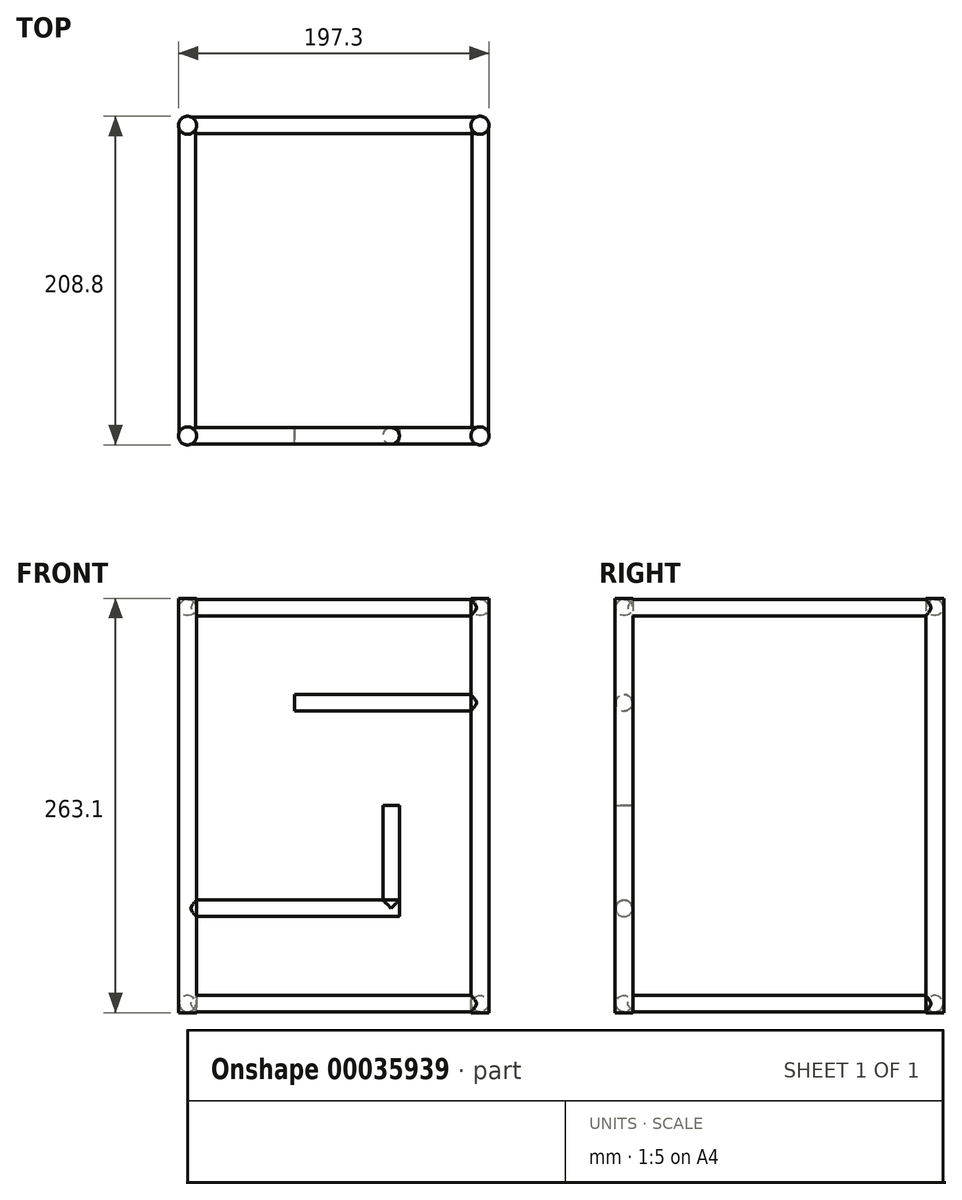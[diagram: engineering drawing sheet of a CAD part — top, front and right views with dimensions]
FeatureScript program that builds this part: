
annotation { "Feature Type Name" : "Feature", "Feature Type Description" : "" }
export const myFeature = defineFeature(function(context is Context, id is Id, definition is map)
    precondition{}
    {
        {
            var Q0;
            Q0=qCreatedBy(makeId("Front.planeOp"),FACE);
            var sketch = newSketch(context, id + "F0", { "sketchPlane" : qUnion([Q0])});
            skLineSegment(sketch, "E0.rect.bottom", {"start": v(98.65, -131.55) * mm, "end": v(-98.65, -131.55) * mm, "construction": true});
            skLineSegment(sketch, "E0.rect.top", {"start": v(98.65, 131.55) * mm, "end": v(-98.65, 131.55) * mm, "construction": true});
            skLineSegment(sketch, "E0.rect.left", {"start": v(98.65, -131.55) * mm, "end": v(98.65, 131.55) * mm, "construction": true});
            skLineSegment(sketch, "E0.rect.right", {"start": v(-98.65, -131.55) * mm, "end": v(-98.65, 131.55) * mm, "construction": true});
            skPoint(sketch, "E0.rect.middle", {"position": v(0, 0) * mm});
            skLineSegment(sketch, "E1.rect.bottom", {"start": v(87.15, -120.05) * mm, "end": v(-87.15, -120.05) * mm, "construction": true});
            skLineSegment(sketch, "E1.rect.top", {"start": v(87.15, 120.05) * mm, "end": v(-87.15, 120.05) * mm, "construction": true});
            skLineSegment(sketch, "E1.rect.left", {"start": v(87.15, -120.05) * mm, "end": v(87.15, 120.05) * mm, "construction": true});
            skLineSegment(sketch, "E1.rect.right", {"start": v(-87.15, -120.05) * mm, "end": v(-87.15, 120.05) * mm, "construction": true});
            skSolve(sketch);
        }
        {
            var Q0;
            Q0=sQuery(id+"F0.wireOp",VERTEX,"E0.rect.bottom.start");
            var Q1;
            Q1=qCreatedBy(makeId("Top.planeOp"),FACE);
            cPlane(context, id + "F1", {"entities" : qUnion([Q0, Q1]), "cplaneType" : CPlaneType.PLANE_POINT, "offset" : 150 * mm, "width" : 150 * mm, "height" : 150 * mm});
        }
        {
            var Q0;
            Q0=qCreatedBy(id+"F1.planeOp",FACE);
            var sketch = newSketch(context, id + "F2", { "sketchPlane" : qUnion([Q0])});
            skCircle(sketch, "E2", {"center": v(-92.9, 0) * mm, "radius": 5.75 * mm});
            skPoint(sketch, "E3", {"position": v(-98.65, 0) * mm});
            skPoint(sketch, "E4", {"position": v(-87.15, 0) * mm});
            skSolve(sketch);
        }
        {
            var Q0;
            Q0=makeQuery(id+"F2.imprint","IMPRINT",FACE,{"disambiguationData":[TD([[makeQuery(id+"F2.imprint","IMPRINT",EDGE,{"derivedFrom":sQuery(id+"F2.wireOp",EDGE,"E2")}),1.0]])]});
            extrude(context, id + "F3", {"entities" : qUnion([Q0]), "depth" : 263.1 * mm});
        }
        {
            var Q0;
            Q0=makeQuery(id+"F3.opExtrude","SWEPT_BODY",BODY,{"disambiguationData":[OSD([sQuery(id+"F2.wireOp",EDGE,"E2")])]});
            var Q1;
            Q1=qCreatedBy(makeId("Right.planeOp"),FACE);
            mirror(context, id + "F4", {"entities" : qUnion([Q0]), "mirrorPlane" : qUnion([Q1])});
        }
        {
            var Q0;
            Q0=qCreatedBy(makeId("Right.planeOp"),FACE);
            var sketch = newSketch(context, id + "F5", { "sketchPlane" : qUnion([Q0])});
            skPoint(sketch, "E5", {"position": v(0, 120.05) * mm});
            skPoint(sketch, "E6", {"position": v(0, 131.55) * mm});
            skCircle(sketch, "E7", {"center": v(0, 125.8) * mm, "radius": 5.75 * mm, "construction": true});
            skCircle(sketch, "E8.0", {"center": v(0, 125.8) * mm, "radius": 5.25 * mm});
            skSolve(sketch);
        }
        {
            var Q0;
            Q0=makeQuery(id+"F5.imprint","IMPRINT",FACE,{"disambiguationData":[TD([[makeQuery(id+"F5.imprint","IMPRINT",EDGE,{"derivedFrom":sQuery(id+"F5.wireOp",EDGE,"E8.0")}),1.0]])]});
            var Q1;
            Q1=makeQuery(id+"F4.opPattern","COPY",FACE,{"derivedFrom":makeQuery(id+"F3.opExtrude","SWEPT_FACE",FACE,{"disambiguationData":[OSD([sQuery(id+"F2.wireOp",EDGE,"E2")])]}),"instanceName":"1"});
            var Q2;
            Q2=makeQuery(id+"F3.opExtrude","SWEPT_FACE",FACE,{"disambiguationData":[OSD([sQuery(id+"F2.wireOp",EDGE,"E2")])]});
            extrude(context, id + "F6", {"entities" : qUnion([Q0]), "endBound" : BoundingType.UP_TO_SURFACE, "endBoundEntityFace" : qUnion([Q1]), "depth" : 25 * mm, "hasSecondDirection" : true, "secondDirectionBound" : SecondDirectionBoundingType.UP_TO_SURFACE, "secondDirectionOppositeDirection" : true, "secondDirectionBoundEntityFace" : qUnion([Q2]), "secondDirectionDepth" : 25 * mm});
        }
        {
            var Q0;
            Q0=makeQuery(id+"F6.opExtrude","SWEPT_BODY",BODY,{"disambiguationData":[OSD([sQuery(id+"F5.wireOp",EDGE,"E8.0")])]});
            var Q1;
            Q1=qCreatedBy(makeId("Top.planeOp"),FACE);
            mirror(context, id + "F7", {"entities" : qUnion([Q0]), "mirrorPlane" : qUnion([Q1])});
        }
        {
            var Q0;
            Q0=qCreatedBy(makeId("Front.planeOp"),FACE);
            cPlane(context, id + "F8", {"entities" : qUnion([Q0]), "cplaneType" : CPlaneType.OFFSET, "offset" : 98.65 * mm, "oppositeDirection" : true, "width" : 150 * mm, "height" : 150 * mm});
        }
        {
            var Q0;
            Q0=makeQuery(id+"F6.opExtrude","SWEPT_BODY",BODY,{"disambiguationData":[OSD([sQuery(id+"F5.wireOp",EDGE,"E8.0")])]});
            var Q1;
            Q1=makeQuery(id+"F7.opPattern","COPY",BODY,{"derivedFrom":makeQuery(id+"F6.opExtrude","SWEPT_BODY",BODY,{"disambiguationData":[OSD([sQuery(id+"F5.wireOp",EDGE,"E8.0")])]}),"instanceName":"1"});
            var Q2;
            Q2=makeQuery(id+"F4.opPattern","COPY",BODY,{"derivedFrom":makeQuery(id+"F3.opExtrude","SWEPT_BODY",BODY,{"disambiguationData":[OSD([sQuery(id+"F2.wireOp",EDGE,"E2")])]}),"instanceName":"1"});
            var Q3;
            Q3=makeQuery(id+"F3.opExtrude","SWEPT_BODY",BODY,{"disambiguationData":[OSD([sQuery(id+"F2.wireOp",EDGE,"E2")])]});
            var Q4;
            Q4=qCreatedBy(id+"F8.planeOp",FACE);
            mirror(context, id + "F9", {"entities" : qUnion([Q0, Q1, Q2, Q3]), "mirrorPlane" : qUnion([Q4])});
        }
        {
            var Q0;
            Q0=qCreatedBy(id+"F8.planeOp",FACE);
            var sketch = newSketch(context, id + "F10", { "sketchPlane" : qUnion([Q0])});
            skCircle(sketch, "E9", {"center": v(92.9, 125.8) * mm, "radius": 5.75 * mm, "construction": true});
            skLineSegment(sketch, "E10", {"start": v(87.15, 131.55) * mm, "end": v(87.15, 86.64) * mm, "construction": true});
            skPoint(sketch, "E11", {"position": v(87.15, 125.8) * mm});
            skPoint(sketch, "E12", {"position": v(98.65, 125.8) * mm});
            skLineSegment(sketch, "E13", {"start": v(98.65, 115.43) * mm, "end": v(98.65, 131.55) * mm, "construction": true});
            skLineSegment(sketch, "E14", {"start": v(98.65, 131.55) * mm, "end": v(87.15, 131.55) * mm, "construction": true});
            skPoint(sketch, "E15", {"position": v(92.9, 131.55) * mm});
            skCircle(sketch, "E16.0", {"center": v(92.9, 125.8) * mm, "radius": 5.25 * mm});
            skSolve(sketch);
        }
        {
            var Q0;
            Q0=makeQuery(id+"F10.imprint","IMPRINT",FACE,{"disambiguationData":[TD([[makeQuery(id+"F10.imprint","IMPRINT",EDGE,{"derivedFrom":sQuery(id+"F10.wireOp",EDGE,"E16.0")}),1.0]])]});
            var Q1;
            Q1=makeQuery(id+"F4.opPattern","COPY",FACE,{"derivedFrom":makeQuery(id+"F3.opExtrude","SWEPT_FACE",FACE,{"disambiguationData":[OSD([sQuery(id+"F2.wireOp",EDGE,"E2")])]}),"instanceName":"1"});
            var Q2;
            Q2=makeQuery(id+"F9.opPattern","COPY",FACE,{"derivedFrom":makeQuery(id+"F4.opPattern","COPY",FACE,{"derivedFrom":makeQuery(id+"F3.opExtrude","SWEPT_FACE",FACE,{"disambiguationData":[OSD([sQuery(id+"F2.wireOp",EDGE,"E2")])]}),"instanceName":"1"}),"instanceName":"1"});
            extrude(context, id + "F11", {"entities" : qUnion([Q0]), "endBound" : BoundingType.UP_TO_SURFACE, "endBoundEntityFace" : qUnion([Q1]), "depth" : 25 * mm, "hasSecondDirection" : true, "secondDirectionBound" : SecondDirectionBoundingType.UP_TO_SURFACE, "secondDirectionOppositeDirection" : true, "secondDirectionBoundEntityFace" : qUnion([Q2]), "secondDirectionDepth" : 25 * mm});
        }
        {
            var Q0;
            Q0=makeQuery(id+"F11.opExtrude","SWEPT_BODY",BODY,{"disambiguationData":[OSD([sQuery(id+"F10.wireOp",EDGE,"E16.0")])]});
            var Q1;
            Q1=qCreatedBy(makeId("Top.planeOp"),FACE);
            mirror(context, id + "F12", {"entities" : qUnion([Q0]), "mirrorPlane" : qUnion([Q1])});
        }
        {
            var Q0;
            Q0=makeQuery(id+"F11.opExtrude","SWEPT_BODY",BODY,{"disambiguationData":[OSD([sQuery(id+"F10.wireOp",EDGE,"E16.0")])]});
            var Q1;
            Q1=makeQuery(id+"F12.opPattern","COPY",BODY,{"derivedFrom":makeQuery(id+"F11.opExtrude","SWEPT_BODY",BODY,{"disambiguationData":[OSD([sQuery(id+"F10.wireOp",EDGE,"E16.0")])]}),"instanceName":"1"});
            var Q2;
            Q2=qCreatedBy(makeId("Right.planeOp"),FACE);
            mirror(context, id + "F13", {"entities" : qUnion([Q0, Q1]), "mirrorPlane" : qUnion([Q2])});
        }
        {
            var Q0;
            Q0=qCreatedBy(makeId("Right.planeOp"),FACE);
            var sketch = newSketch(context, id + "F14", { "sketchPlane" : qUnion([Q0])});
            skLineSegment(sketch, "E17", {"start": v(0, 131.55) * mm, "end": v(0, -131.55) * mm, "construction": true});
            skCircle(sketch, "E18", {"center": v(0, -65.3) * mm, "radius": 5.25 * mm});
            skPoint(sketch, "E19", {"position": v(0, -60.05) * mm});
            skSolve(sketch);
        }
        {
            var Q0;
            Q0 = qSketchRegion(id + "F14", true);
            var Q1;
            Q1=makeQuery(id+"F3.opExtrude","SWEPT_FACE",FACE,{"disambiguationData":[OSD([sQuery(id+"F2.wireOp",EDGE,"E2")])]});
            extrude(context, id + "F15", {"entities" : qUnion([Q0]), "operationType" : NewBodyOperationType.ADD, "endBound" : BoundingType.UP_TO_SURFACE, "oppositeDirection" : true, "endBoundEntityFace" : qUnion([Q1]), "depth" : 25 * mm, "hasSecondDirection" : true, "secondDirectionOppositeDirection" : false, "secondDirectionDepth" : 41.66 * mm});
        }
        {
            var Q0;
            Q0=qCreatedBy(makeId("Top.planeOp"),FACE);
            var sketch = newSketch(context, id + "F16", { "sketchPlane" : qUnion([Q0])});
            skLineSegment(sketch, "E20", {"start": v(-98.65, 0) * mm, "end": v(98.65, 0) * mm, "construction": true});
            skLineSegment(sketch, "E21.0", {"start": v(41.66, 5.25) * mm, "end": v(41.66, -5.25) * mm, "construction": true});
            skCircle(sketch, "E22", {"center": v(41.66, 0) * mm, "radius": 5.25 * mm, "construction": true});
            skCircle(sketch, "E23", {"center": v(36.4, 0) * mm, "radius": 5.25 * mm});
            skSolve(sketch);
        }
        {
            var Q0;
            Q0=makeQuery(id+"F16.imprint","IMPRINT",FACE,{"disambiguationData":[TD([[makeQuery(id+"F16.imprint","IMPRINT",EDGE,{"derivedFrom":sQuery(id+"F16.wireOp",EDGE,"E23")}),1.0]])]});
            var Q1;
            Q1=makeQuery(id+"F15.opExtrude","SWEPT_FACE",FACE,{"disambiguationData":[OSD([sQuery(id+"F14.wireOp",EDGE,"E18")])]});
            extrude(context, id + "F17", {"entities" : qUnion([Q0]), "endBound" : BoundingType.UP_TO_SURFACE, "oppositeDirection" : true, "endBoundEntityFace" : qUnion([Q1]), "depth" : 25 * mm});
        }
        {
            var Q0;
            Q0=qCreatedBy(makeId("Right.planeOp"),FACE);
            var sketch = newSketch(context, id + "F18", { "sketchPlane" : qUnion([Q0])});
            skLineSegment(sketch, "E24.0", {"start": v(0, -120.05) * mm, "end": v(0, 120.05) * mm, "construction": true});
            skPoint(sketch, "E25.0", {"position": v(0, 131.55) * mm});
            skCircle(sketch, "E26", {"center": v(0, 65.3) * mm, "radius": 5.25 * mm});
            skPoint(sketch, "E27", {"position": v(0, 60.05) * mm});
            skSolve(sketch);
        }
        {
            var Q0;
            Q0 = qSketchRegion(id + "F18", true);
            var Q1;
            Q1=makeQuery(id+"F3.opExtrude","SWEPT_FACE",FACE,{"disambiguationData":[OSD([sQuery(id+"F2.wireOp",EDGE,"E2")])]});
            var Q2;
            Q2=makeQuery(id+"F4.opPattern","COPY",FACE,{"derivedFrom":makeQuery(id+"F3.opExtrude","SWEPT_FACE",FACE,{"disambiguationData":[OSD([sQuery(id+"F2.wireOp",EDGE,"E2")])]}),"instanceName":"1"});
            extrude(context, id + "F19", {"entities" : qUnion([Q0]), "operationType" : NewBodyOperationType.ADD, "oppositeDirection" : true, "endBoundEntityFace" : qUnion([Q1]), "depth" : 25 * mm, "hasSecondDirection" : true, "secondDirectionBound" : SecondDirectionBoundingType.UP_TO_SURFACE, "secondDirectionOppositeDirection" : false, "secondDirectionBoundEntityFace" : qUnion([Q2]), "secondDirectionDepth" : 25 * mm});
        }
    });
